# Revit family: Gripple Trapeze Plus
name_source: partatom
category: Specialty Equipment
revit_build: Autodesk Revit 2017 (Build: 20160606_1515(x64)
units: mm (PartAtom-declared; Revit-internal decimal feet)

## family parameters
Always vertical = Yes
Cut with Voids When Loaded = No
Part Type = Normal
Room Calculation Point = No
Round Connector Dimension = Use Diameter
Shared = Yes
Work Plane-Based = Yes

## types (3) — shared parameters
KNW = 4 mm  [stored 0.0131234 ft]
MTL = 20 mm  [stored 0.0656168 ft]
Manufacturer = Gripple Ltd
URL = http://www.gripple.co.uk
zero-valued in all types: Default Elevation

## per-type parameters (varying)
| type | AC | AF | BH | BNT | HH | Hanger SWL (kg) | KND | MTD | Model | TTD | UL | WD | WD/2 |
| MTZ3 | 20 mm  [stored 0.0656168 ft] | 17 mm | 34 mm | 43 mm | 15 mm  [stored 0.0492126 ft] | 90kg | 10 mm  [stored 0.0328084 ft] | 10 mm  [stored 0.0328084 ft] | Trapeze Plus No3 | 8 mm  [stored 0.0262467 ft] | 63 mm  [stored 0.206693 ft] | 3 mm  [stored 0.00984252 ft] | 2 mm  [stored 0.00656168 ft] |
| MTZ2 | 17 mm | 15 mm  [stored 0.0492126 ft] | 28 mm  [stored 0.0918635 ft] | 39 mm  [stored 0.127953 ft] | 14 mm  [stored 0.0459318 ft] | 45kg | 10 mm  [stored 0.0328084 ft] | 8 mm  [stored 0.0262467 ft] | Trapeze Plus No2 | 7 mm  [stored 0.0229659 ft] | 59 mm  [stored 0.19357 ft] | 2 mm  [stored 0.00656168 ft] | 1 mm  [stored 0.00328084 ft] |
| MTZ4 | 25 mm  [stored 0.082021 ft] | 22 mm  [stored 0.0721785 ft] | 38 mm  [stored 0.124672 ft] | 54 mm | 18 mm  [stored 0.0590551 ft] | 225kg | 14 mm  [stored 0.0459318 ft] | 10 mm  [stored 0.0328084 ft] | Trapeze Plus No4 | 10 mm  [stored 0.0328084 ft] | 74 mm | 5 mm  [stored 0.0164042 ft] | 2 mm  [stored 0.00656168 ft] |

note: column(s) folded — value = type name in every type: Assembly Code

note: [stored X ft] marks values corroborated as IEEE doubles in the binary element streams (Revit-internal decimal feet)

## geometry (parser evidence)
native form markers: Blend x4, Sweep x1
no freeform markers — native parametric forms only
